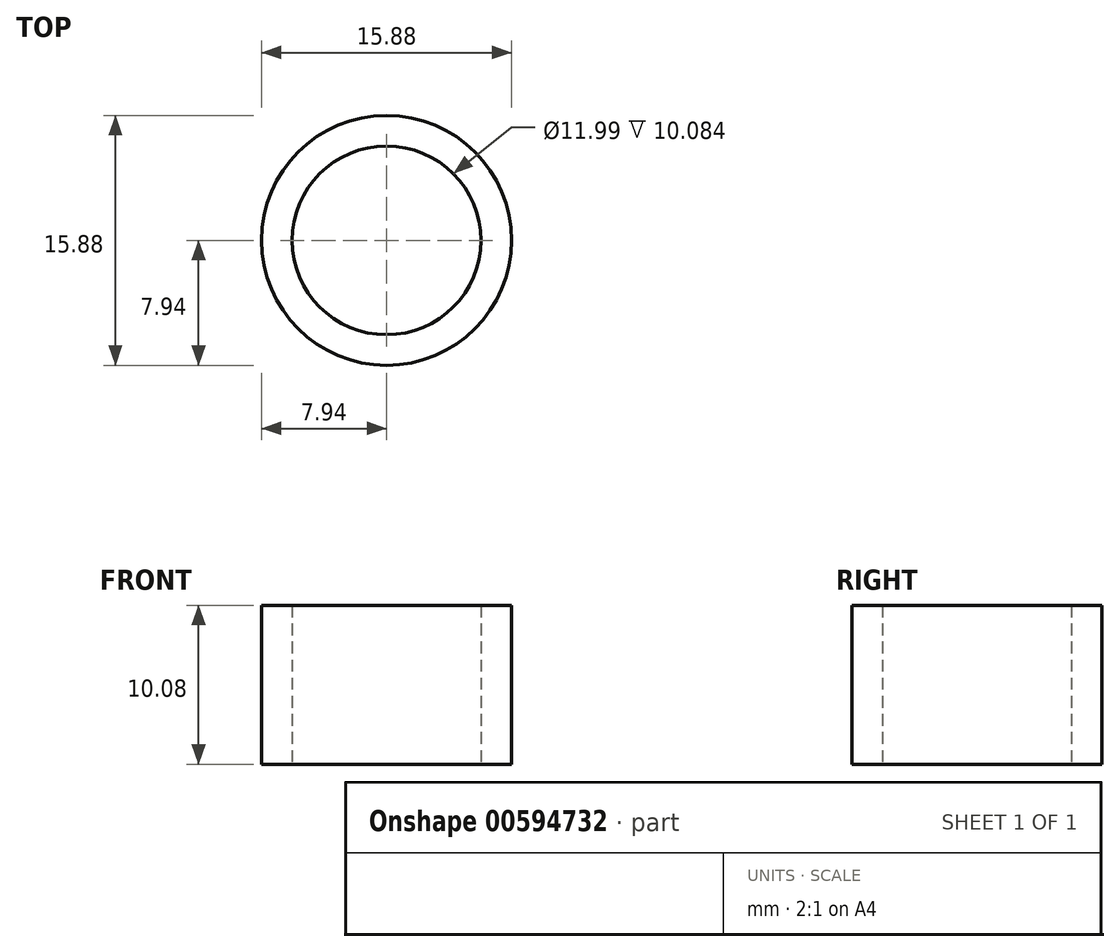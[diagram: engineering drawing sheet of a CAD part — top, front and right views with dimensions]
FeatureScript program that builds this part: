
annotation { "Feature Type Name" : "Feature", "Feature Type Description" : "" }
export const myFeature = defineFeature(function(context is Context, id is Id, definition is map)
    precondition{}
    {
        {
            var Q0;
            Q0=qCreatedBy(makeId("Top.planeOp"),FACE);
            var sketch = newSketch(context, id + "F0", { "sketchPlane" : qUnion([Q0])});
            skCircle(sketch, "E0", {"center": v(0, 0) * mm, "radius": 6 * mm});
            skCircle(sketch, "E1", {"center": v(0, 0) * mm, "radius": 7.94 * mm});
            skSolve(sketch);
        }
        {
            var Q0;
            Q0=makeQuery(id+"F0.imprint","IMPRINT",FACE,{"disambiguationData":[TD([[makeQuery(id+"F0.imprint","IMPRINT",EDGE,{"derivedFrom":sQuery(id+"F0.wireOp",EDGE,"E0")}),-1.0]])]});
            extrude(context, id + "F1", {"entities" : qUnion([Q0]), "depth" : 10.08 * mm, "offsetDistance" : 25.4 * mm});
        }
    });
